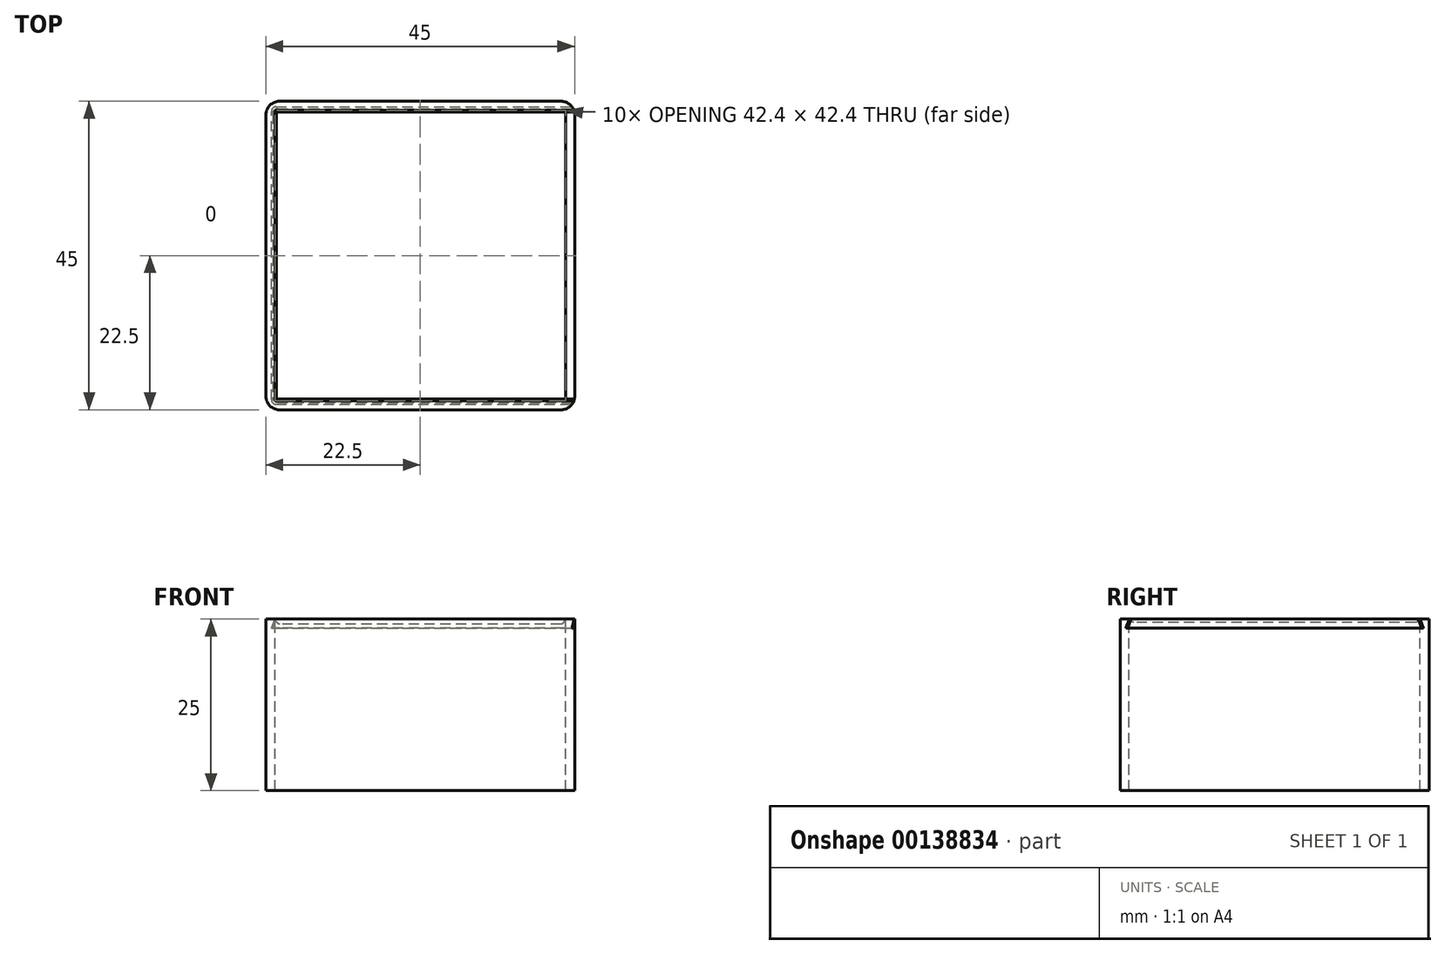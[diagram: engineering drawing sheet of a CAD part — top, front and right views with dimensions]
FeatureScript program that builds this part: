
annotation { "Feature Type Name" : "Feature", "Feature Type Description" : "" }
export const myFeature = defineFeature(function(context is Context, id is Id, definition is map)
    precondition{}
    {
        {
            var Q0;
            Q0=qCreatedBy(makeId("Top.planeOp"),FACE);
            var sketch = newSketch(context, id + "F0", { "sketchPlane" : qUnion([Q0])});
            skLineSegment(sketch, "E0.bottom", {"start": v(-22.5, 22.5) * mm, "end": v(22.5, 22.5) * mm});
            skLineSegment(sketch, "E0.top", {"start": v(-22.5, -22.5) * mm, "end": v(22.5, -22.5) * mm});
            skLineSegment(sketch, "E0.left", {"start": v(-22.5, 22.5) * mm, "end": v(-22.5, -22.5) * mm});
            skLineSegment(sketch, "E0.right", {"start": v(22.5, 22.5) * mm, "end": v(22.5, -22.5) * mm});
            skPoint(sketch, "E0.middle", {"position": v(0, 0) * mm});
            skSolve(sketch);
        }
        {
            var Q0;
            Q0 = qSketchRegion(id + "F0", true);
            extrude(context, id + "F1", {"entities" : qUnion([Q0]), "depth" : 45 * mm});
        }
        {
            var Q0;
            Q0=makeQuery(id+"F1.opExtrude","SWEPT_EDGE",EDGE,{"disambiguationData":[OSD([sQuery(id+"F0.wireOp",EDGE,"E0.top"),sQuery(id+"F0.wireOp",EDGE,"E0.left")])]});
            var Q1;
            Q1=makeQuery(id+"F1.opExtrude","SWEPT_EDGE",EDGE,{"disambiguationData":[OSD([sQuery(id+"F0.wireOp",EDGE,"E0.bottom"),sQuery(id+"F0.wireOp",EDGE,"E0.left")])]});
            var Q2;
            Q2=makeQuery(id+"F1.opExtrude","SWEPT_EDGE",EDGE,{"disambiguationData":[OSD([sQuery(id+"F0.wireOp",EDGE,"E0.top"),sQuery(id+"F0.wireOp",EDGE,"E0.right")])]});
            var Q3;
            Q3=makeQuery(id+"F1.opExtrude","SWEPT_EDGE",EDGE,{"disambiguationData":[OSD([sQuery(id+"F0.wireOp",EDGE,"E0.bottom"),sQuery(id+"F0.wireOp",EDGE,"E0.right")])]});
            var Q4;
            Q4=makeQuery(id+"F1.opExtrude","CAP_FACE",FACE,{"disambiguationData":[OSD([sQuery(id+"F0.wireOp",EDGE,"E0.bottom"),sQuery(id+"F0.wireOp",EDGE,"E0.top"),sQuery(id+"F0.wireOp",EDGE,"E0.left"),sQuery(id+"F0.wireOp",EDGE,"E0.right")])],"isStart":true});
            fillet(context, id + "F2", {"entities" : qUnion([Q0, Q1, Q2, Q3, Q4]), "radius" : 2 * mm, "tangentPropagation" : true, "allowEdgeOverflow" : false});
        }
        {
            var Q0;
            Q0=makeQuery(id+"F1.opExtrude","SWEPT_FACE",FACE,{"disambiguationData":[OSD([sQuery(id+"F0.wireOp",EDGE,"E0.right")])]});
            var sketch = newSketch(context, id + "F3", { "sketchPlane" : qUnion([Q0])});
            skLineSegment(sketch, "E1.bottom", {"start": v(-21.7, 45) * mm, "end": v(21.7, 45) * mm});
            skLineSegment(sketch, "E1.top", {"start": v(-21.7, 43.7) * mm, "end": v(21.7, 43.7) * mm});
            skLineSegment(sketch, "E1.left", {"start": v(-21.7, 45) * mm, "end": v(-21.7, 43.7) * mm});
            skLineSegment(sketch, "E1.right", {"start": v(21.7, 45) * mm, "end": v(21.7, 43.7) * mm});
            skPoint(sketch, "E1.middle", {"position": v(0, 44.35) * mm});
            skSolve(sketch);
        }
        {
            var Q0;
            Q0 = qSketchRegion(id + "F3", true);
            extrude(context, id + "F4", {"entities" : qUnion([Q0]), "oppositeDirection" : true, "depth" : 44.2 * mm});
        }
        {
            var Q0;
            Q0=makeQuery(id+"F4.opExtrude","CAP_EDGE",EDGE,{"disambiguationData":[OSD([sQuery(id+"F3.wireOp",EDGE,"E1.left")])],"isStart":false});
            var Q1;
            Q1=makeQuery(id+"F4.opExtrude","CAP_EDGE",EDGE,{"disambiguationData":[OSD([sQuery(id+"F3.wireOp",EDGE,"E1.right")])],"isStart":false});
            fillet(context, id + "F5", {"entities" : qUnion([Q0, Q1]), "radius" : 0.7 * mm, "tangentPropagation" : true, "allowEdgeOverflow" : false});
        }
        {
            var Q0;
            Q0=makeQuery(id+"F4.opExtrude","SWEPT_EDGE",EDGE,{"disambiguationData":[OSD([sQuery(id+"F3.wireOp",EDGE,"E1.bottom"),sQuery(id+"F3.wireOp",EDGE,"E1.left")])]});
            var Q1;
            Q1=makeQuery(id+"F4.opExtrude","CAP_EDGE",EDGE,{"disambiguationData":[OSD([sQuery(id+"F3.wireOp",EDGE,"E1.bottom")])],"isStart":false});
            var Q2;
            Q2=makeQuery(id+"F4.opExtrude","SWEPT_EDGE",EDGE,{"disambiguationData":[OSD([sQuery(id+"F3.wireOp",EDGE,"E1.bottom"),sQuery(id+"F3.wireOp",EDGE,"E1.right")])]});
            chamfer(context, id + "F6", {"entities" : qUnion([Q0, Q1, Q2]), "chamferType" : ChamferType.TWO_OFFSETS, "width1" : 0.5 * mm, "oppositeDirection" : false, "width2" : 1.3 * mm, "tangentPropagation" : true});
        }
        {
            var Q0;
            Q0=makeQuery(id+"F4.opExtrude","SWEPT_BODY",BODY,{"disambiguationData":[OSD([sQuery(id+"F3.wireOp",EDGE,"E1.bottom"),sQuery(id+"F3.wireOp",EDGE,"E1.top"),sQuery(id+"F3.wireOp",EDGE,"E1.left"),sQuery(id+"F3.wireOp",EDGE,"E1.right")])]});
            var Q1;
            Q1=makeQuery(id+"F1.opExtrude","SWEPT_BODY",BODY,{"disambiguationData":[OSD([sQuery(id+"F0.wireOp",EDGE,"E0.bottom"),sQuery(id+"F0.wireOp",EDGE,"E0.top"),sQuery(id+"F0.wireOp",EDGE,"E0.left"),sQuery(id+"F0.wireOp",EDGE,"E0.right")])]});
            booleanBodies(context, id + "F7", {"operationType" : BooleanOperationType.SUBTRACTION, "tools" : qUnion([Q0]), "targets" : qUnion([Q1])});
        }
        {
            var Q0;
            Q0=makeQuery(id+"F1.opExtrude","CAP_FACE",FACE,{"disambiguationData":[OSD([sQuery(id+"F0.wireOp",EDGE,"E0.bottom"),sQuery(id+"F0.wireOp",EDGE,"E0.top"),sQuery(id+"F0.wireOp",EDGE,"E0.left"),sQuery(id+"F0.wireOp",EDGE,"E0.right")])],"isStart":false});
            var sketch = newSketch(context, id + "F8", { "sketchPlane" : qUnion([Q0])});
            skLineSegment(sketch, "E2.bottom", {"start": v(-20.5, 21.2) * mm, "end": v(20.5, 21.2) * mm});
            skLineSegment(sketch, "E2.top", {"start": v(-20.5, -21.2) * mm, "end": v(20.5, -21.2) * mm});
            skLineSegment(sketch, "E2.left", {"start": v(-21.2, 20.5) * mm, "end": v(-21.2, -20.5) * mm});
            skLineSegment(sketch, "E2.right", {"start": v(21.2, 20.5) * mm, "end": v(21.2, -20.5) * mm});
            skPoint(sketch, "E2.middle", {"position": v(0, 0) * mm});
            skPoint(sketch, "E3.visualSharp", {"position": v(-21.2, -21.2) * mm});
            skArc(sketch, "E3.filletArc", {"start": v(-21.2, -20.5) * mm, "mid": v(-21, -21) * mm, "end": v(-20.5, -21.2) * mm});
            skPoint(sketch, "E4.visualSharp", {"position": v(-21.2, 21.2) * mm});
            skArc(sketch, "E4.filletArc", {"start": v(-20.5, 21.2) * mm, "mid": v(-21, 21) * mm, "end": v(-21.2, 20.5) * mm});
            skPoint(sketch, "E5.visualSharp", {"position": v(21.2, 21.2) * mm});
            skArc(sketch, "E5.filletArc", {"start": v(21.2, 20.5) * mm, "mid": v(21, 21) * mm, "end": v(20.5, 21.2) * mm});
            skPoint(sketch, "E6.visualSharp", {"position": v(21.2, -21.2) * mm});
            skArc(sketch, "E6.filletArc", {"start": v(20.5, -21.2) * mm, "mid": v(21, -21) * mm, "end": v(21.2, -20.5) * mm});
            skSolve(sketch);
        }
        {
            var Q0;
            Q0 = qSketchRegion(id + "F8", true);
            extrude(context, id + "F9", {"entities" : qUnion([Q0]), "operationType" : NewBodyOperationType.REMOVE, "oppositeDirection" : true, "depth" : (45 - 1.3) * mm});
        }
        {
            var Q0;
            Q0=makeQuery(id+"F9.boolean.opBoolean","COPY",FACE,{"derivedFrom":makeQuery(id+"F9.opExtrude","CAP_FACE",FACE,{"disambiguationData":[OSD([sQuery(id+"F8.wireOp",EDGE,"E2.bottom"),sQuery(id+"F8.wireOp",EDGE,"E2.top"),sQuery(id+"F8.wireOp",EDGE,"E2.left"),sQuery(id+"F8.wireOp",EDGE,"E2.right"),sQuery(id+"F8.wireOp",EDGE,"E3.filletArc"),sQuery(id+"F8.wireOp",EDGE,"E4.filletArc"),sQuery(id+"F8.wireOp",EDGE,"E5.filletArc"),sQuery(id+"F8.wireOp",EDGE,"E6.filletArc")])],"isStart":false})});
            fillet(context, id + "F10", {"entities" : qUnion([Q0]), "radius" : 0.7 * mm, "tangentPropagation" : true, "allowEdgeOverflow" : false});
        }
        {
            var Q0;
            Q0=makeQuery(id+"F1.opExtrude","SWEPT_FACE",FACE,{"disambiguationData":[OSD([sQuery(id+"F0.wireOp",EDGE,"E0.right")])]});
            var sketch = newSketch(context, id + "F11", { "sketchPlane" : qUnion([Q0])});
            skLineSegment(sketch, "E7.bottom", {"start": v(21.4, 45) * mm, "end": v(-21.4, 45) * mm});
            skLineSegment(sketch, "E7.top", {"start": v(21.4, 43.7) * mm, "end": v(-21.4, 43.7) * mm});
            skLineSegment(sketch, "E7.left", {"start": v(21.4, 45) * mm, "end": v(21.4, 43.7) * mm});
            skLineSegment(sketch, "E7.right", {"start": v(-21.4, 45) * mm, "end": v(-21.4, 43.7) * mm});
            skPoint(sketch, "E7.middle", {"position": v(0, 44.35) * mm});
            skSolve(sketch);
        }
        {
            var Q0;
            Q0 = qSketchRegion(id + "F11", true);
            extrude(context, id + "F12", {"entities" : qUnion([Q0]), "oppositeDirection" : true, "depth" : 44 * mm});
        }
        {
            var Q0;
            Q0=makeQuery(id+"F12.opExtrude","CAP_EDGE",EDGE,{"disambiguationData":[OSD([sQuery(id+"F11.wireOp",EDGE,"E7.left")])],"isStart":false});
            var Q1;
            Q1=makeQuery(id+"F12.opExtrude","CAP_EDGE",EDGE,{"disambiguationData":[OSD([sQuery(id+"F11.wireOp",EDGE,"E7.right")])],"isStart":false});
            fillet(context, id + "F13", {"entities" : qUnion([Q0, Q1]), "radius" : 0.7 * mm, "tangentPropagation" : true, "allowEdgeOverflow" : false});
        }
        {
            var Q0;
            Q0=makeQuery(id+"F12.opExtrude","SWEPT_EDGE",EDGE,{"disambiguationData":[OSD([sQuery(id+"F11.wireOp",EDGE,"E7.bottom"),sQuery(id+"F11.wireOp",EDGE,"E7.right")])]});
            var Q1;
            Q1=makeQuery(id+"F12.opExtrude","CAP_EDGE",EDGE,{"disambiguationData":[OSD([sQuery(id+"F11.wireOp",EDGE,"E7.bottom")])],"isStart":false});
            var Q2;
            Q2=makeQuery(id+"F12.opExtrude","SWEPT_EDGE",EDGE,{"disambiguationData":[OSD([sQuery(id+"F11.wireOp",EDGE,"E7.bottom"),sQuery(id+"F11.wireOp",EDGE,"E7.left")])]});
            chamfer(context, id + "F14", {"entities" : qUnion([Q0, Q1, Q2]), "chamferType" : ChamferType.TWO_OFFSETS, "width1" : 0.5 * mm, "oppositeDirection" : false, "width2" : 1.3 * mm, "tangentPropagation" : true});
        }
        {
            var Q0;
            Q0=makeQuery(id+"F12.opExtrude","SWEPT_FACE",FACE,{"disambiguationData":[OSD([sQuery(id+"F11.wireOp",EDGE,"E7.bottom")])]});
            var sketch = newSketch(context, id + "F15", { "sketchPlane" : qUnion([Q0])});
            skLineSegment(sketch, "E8.bottom", {"start": v(20.5, 22.5) * mm, "end": v(-22.5, 22.5) * mm});
            skLineSegment(sketch, "E8.top", {"start": v(20.5, -22.5) * mm, "end": v(-22.5, -22.5) * mm});
            skLineSegment(sketch, "E8.left", {"start": v(22.5, 20.5) * mm, "end": v(22.5, -20.5) * mm});
            skLineSegment(sketch, "E8.right", {"start": v(-22.5, 22.5) * mm, "end": v(-22.5, -22.5) * mm});
            skPoint(sketch, "E8.middle", {"position": v(0, 0) * mm});
            skPoint(sketch, "E9.visualSharp", {"position": v(22.5, -22.5) * mm});
            skArc(sketch, "E9.filletArc", {"start": v(20.5, -22.5) * mm, "mid": v(21.91, -21.91) * mm, "end": v(22.5, -20.5) * mm});
            skPoint(sketch, "E10.visualSharp", {"position": v(22.5, 22.5) * mm});
            skArc(sketch, "E10.filletArc", {"start": v(22.5, 20.5) * mm, "mid": v(21.91, 21.91) * mm, "end": v(20.5, 22.5) * mm});
            skSolve(sketch);
        }
        {
            var Q0;
            Q0 = qSketchRegion(id + "F15", true);
            extrude(context, id + "F16", {"entities" : qUnion([Q0]), "operationType" : NewBodyOperationType.INTERSECT, "oppositeDirection" : true, "depth" : 25 * mm});
        }
    });
